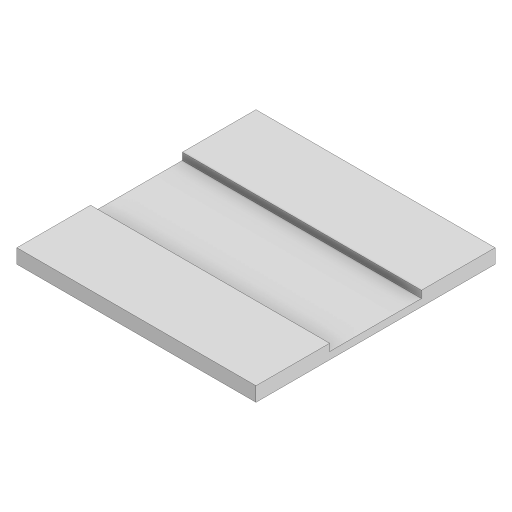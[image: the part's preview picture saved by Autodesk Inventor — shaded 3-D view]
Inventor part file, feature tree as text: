
AUTODESK INVENTOR PART (.ipt)
format: ipt  version: 2023 (Build 270158000, 158)  size: 121,856 bytes
history: native  units: in
note: dims shown in document units (in); Inventor stores cm internally (conversion verified against a paired STEP export)
features: extrude x3, sketch x3, projected_geometry x2
ambient origin geometry x8: Origin, YZ Plane, XZ Plane, XY Plane, X Axis, Y Axis, Z Axis, Center Point
bodies: Solid1 (feature_tree)
feature tree (8):
  extrude  "Extrusion1"  Depth=3937.0079in
  extrude  "Extrusion2"  Depth=118.1102in TaperAngle=0.0deg
  extrude  "Extrusion3"  Depth=1.0in TaperAngle=0.0deg
  sketch  "Sketch1"  dims[d0=3937.0079in d1=3937.0079in]
  sketch  "Sketch2"  dims[d2=118.1102in d3=0.0in d4=118.1102in d5=0.0in]
  projected_geometry  "Projected Loop1"
  sketch  "Sketch3"  dims[d6=7874.0157in d7=1.0in d8=0.0in]
  projected_geometry  "Projected Loop2"
